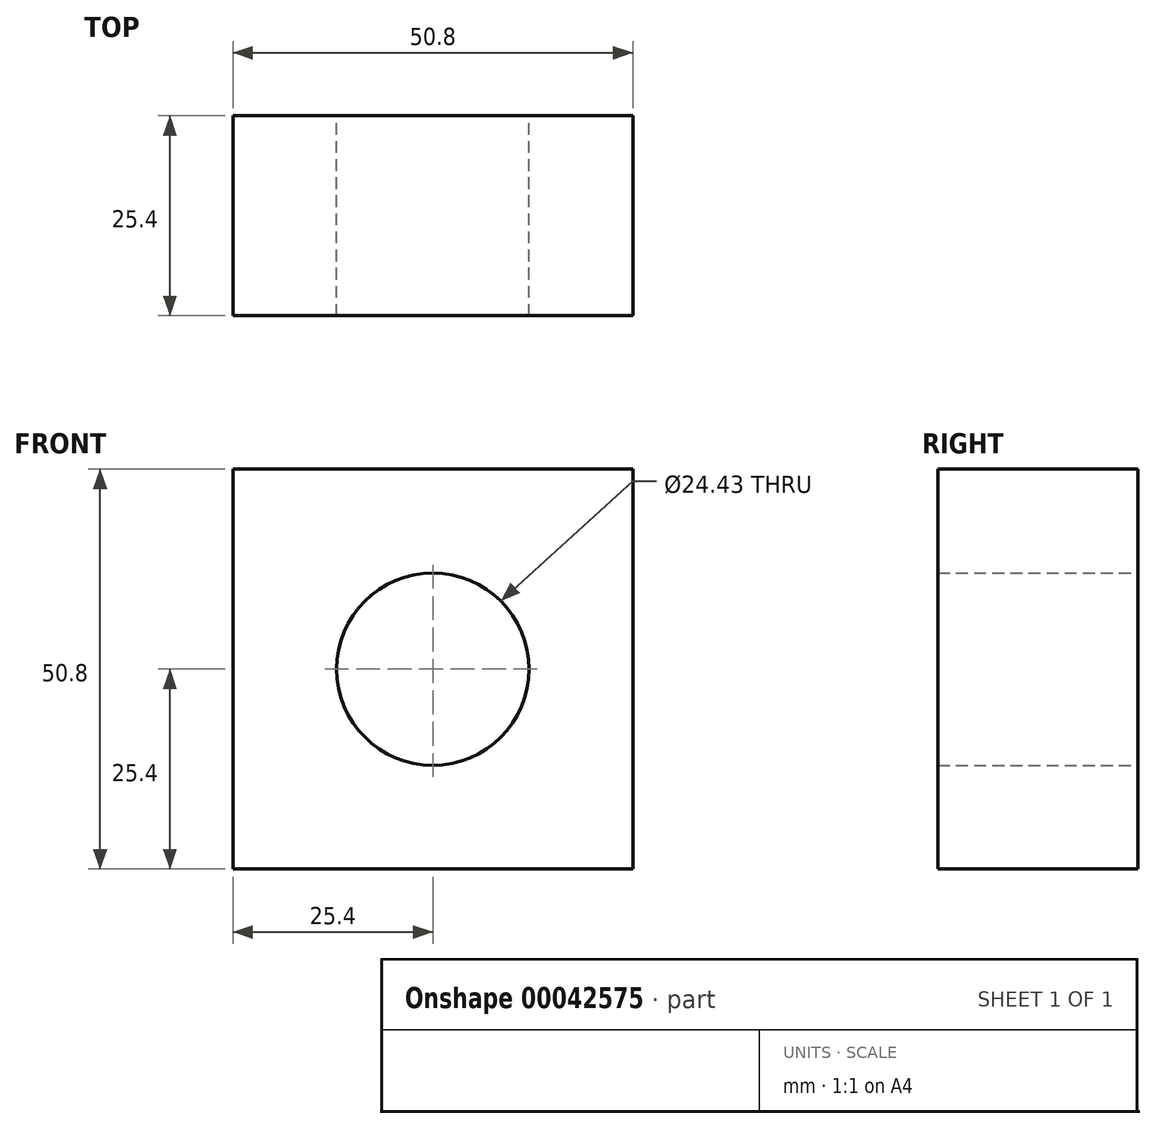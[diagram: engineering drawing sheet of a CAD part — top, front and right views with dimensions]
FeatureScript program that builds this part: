
annotation { "Feature Type Name" : "Feature", "Feature Type Description" : "" }
export const myFeature = defineFeature(function(context is Context, id is Id, definition is map)
    precondition{}
    {
        {
            var Q0;
            Q0=qCreatedBy(makeId("Front.planeOp"),FACE);
            var sketch = newSketch(context, id + "F0", { "sketchPlane" : qUnion([Q0])});
            skLineSegment(sketch, "E0.bottom", {"start": v(0, 0) * mm, "end": v(50.8, 0) * mm});
            skLineSegment(sketch, "E0.top", {"start": v(0, 50.8) * mm, "end": v(50.8, 50.8) * mm});
            skLineSegment(sketch, "E0.left", {"start": v(0, 0) * mm, "end": v(0, 50.8) * mm});
            skLineSegment(sketch, "E0.right", {"start": v(50.8, 0) * mm, "end": v(50.8, 50.8) * mm});
            skCircle(sketch, "E1", {"center": v(25.4, 25.4) * mm, "radius": 12.21 * mm});
            skSolve(sketch);
        }
        {
            var Q0;
            Q0=makeQuery(id+"F0.imprint","IMPRINT",FACE,{"disambiguationData":[TD([[makeQuery(id+"F0.imprint","IMPRINT",EDGE,{"derivedFrom":sQuery(id+"F0.wireOp",EDGE,"E0.bottom")}),1.0]])]});
            extrude(context, id + "F1", {"entities" : qUnion([Q0]), "depth" : 25.4 * mm});
        }
    });
